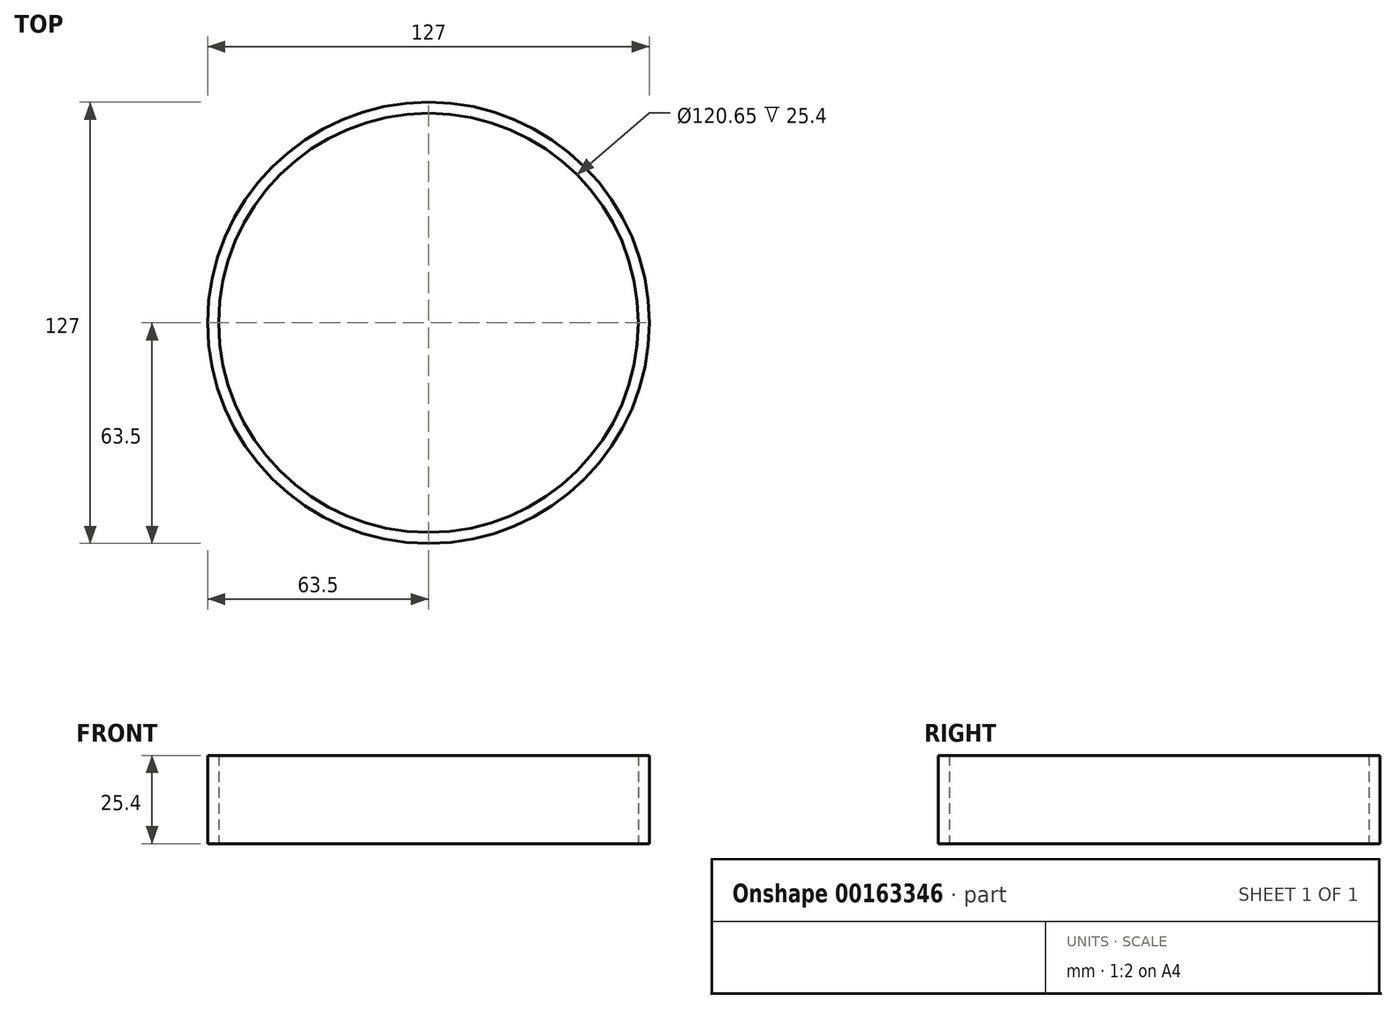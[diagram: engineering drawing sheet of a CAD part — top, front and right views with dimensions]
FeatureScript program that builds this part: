
annotation { "Feature Type Name" : "Feature", "Feature Type Description" : "" }
export const myFeature = defineFeature(function(context is Context, id is Id, definition is map)
    precondition{}
    {
        {
            var Q0;
            Q0=qCreatedBy(makeId("Top.planeOp"),FACE);
            var sketch = newSketch(context, id + "F0", { "sketchPlane" : qUnion([Q0])});
            skCircle(sketch, "E0", {"center": v(0, 0) * mm, "radius": 63.5 * mm});
            skCircle(sketch, "E1", {"center": v(0, 0) * mm, "radius": 60.33 * mm});
            skSolve(sketch);
        }
        {
            var Q0;
            Q0=makeQuery(id+"F0.imprint","IMPRINT",FACE,{"disambiguationData":[TD([[makeQuery(id+"F0.imprint","IMPRINT",EDGE,{"derivedFrom":sQuery(id+"F0.wireOp",EDGE,"E0")}),1.0]])]});
            extrude(context, id + "F1", {"entities" : qUnion([Q0]), "depth" : 25.4 * mm});
        }
    });
